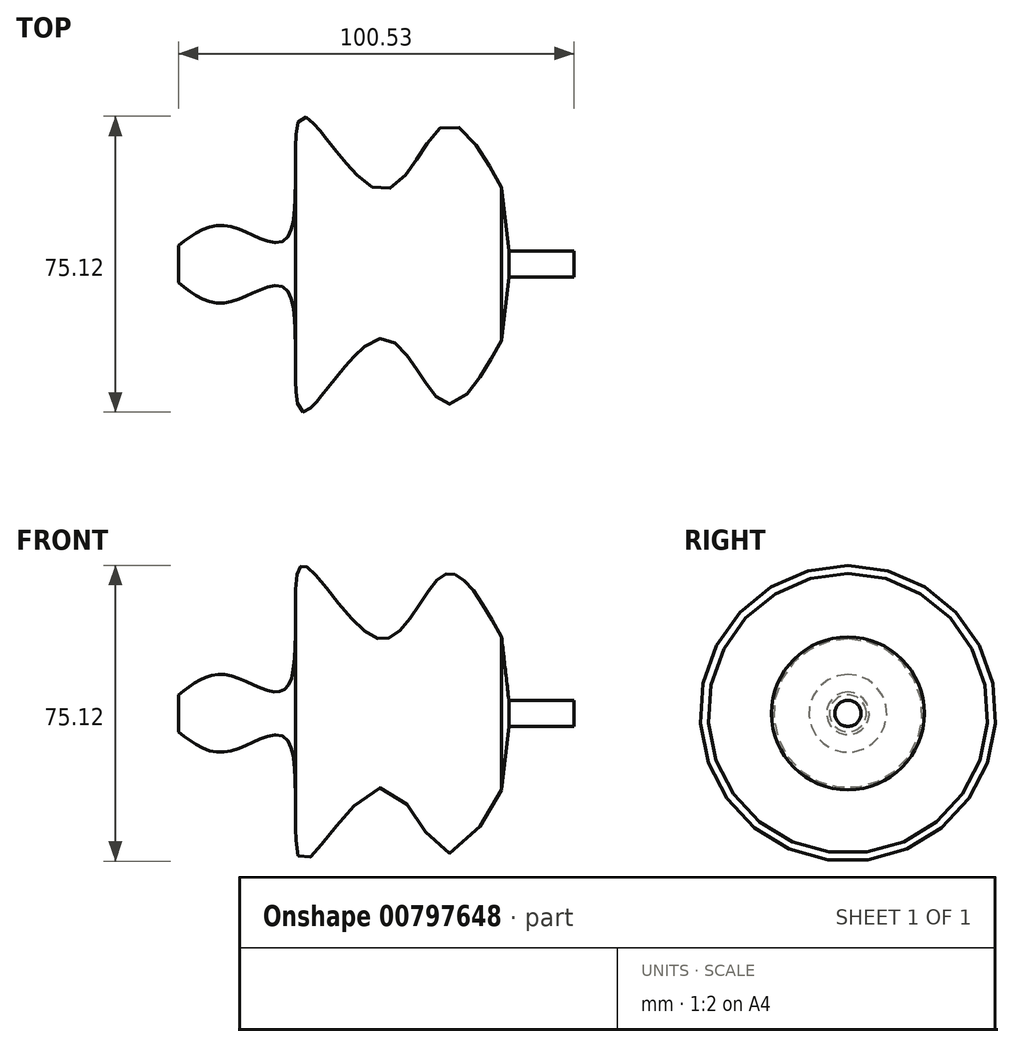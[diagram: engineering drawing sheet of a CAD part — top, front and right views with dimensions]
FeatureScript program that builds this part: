
annotation { "Feature Type Name" : "Feature", "Feature Type Description" : "" }
export const myFeature = defineFeature(function(context is Context, id is Id, definition is map)
    precondition{}
    {
        {
            var Q0;
            Q0=qCreatedBy(makeId("Top.planeOp"),FACE);
            var sketch = newSketch(context, id + "F0", { "sketchPlane" : qUnion([Q0])});
            skFitSpline(sketch, "E0", {"points": [v(21.55, -19.41) * mm, v(6.8, -35.16) * mm, v(-9.11, -18.9) * mm, v(-29.22, -37.5) * mm, v(-32.9, -6.68) * mm, v(-47.82, -9.7) * mm, v(-60.55, -4.67) * mm], "startDerivative": vector(-90.13, -162.84) * mm, "endDerivative": vector(-86.44, 68.38) * mm});
            skLineSegment(sketch, "E1", {"start": v(-60.55, -4.67) * mm, "end": v(-60.55, 0) * mm});
            skLineSegment(sketch, "E2", {"start": v(-60.55, 0) * mm, "end": v(39.98, 0) * mm});
            skLineSegment(sketch, "E3", {"start": v(39.98, 0) * mm, "end": v(39.98, -3.33) * mm});
            skLineSegment(sketch, "E4", {"start": v(39.98, -3.33) * mm, "end": v(23.39, -3.33) * mm});
            skLineSegment(sketch, "E5", {"start": v(23.39, -3.33) * mm, "end": v(21.55, -19.41) * mm});
            skSolve(sketch);
        }
        {
            var Q0;
            Q0 = qSketchRegion(id + "F0", true);
            var Q1;
            Q1=sQuery(id+"F0.wireOp",EDGE,"E2");
            revolve(context, id + "F1", {"surfaceOperationType" : NewSurfaceOperationType.NEW, "entities" : qUnion([Q0]), "axis" : qUnion([Q1]), "revolveType" : RevolveType.FULL});
        }
    });
